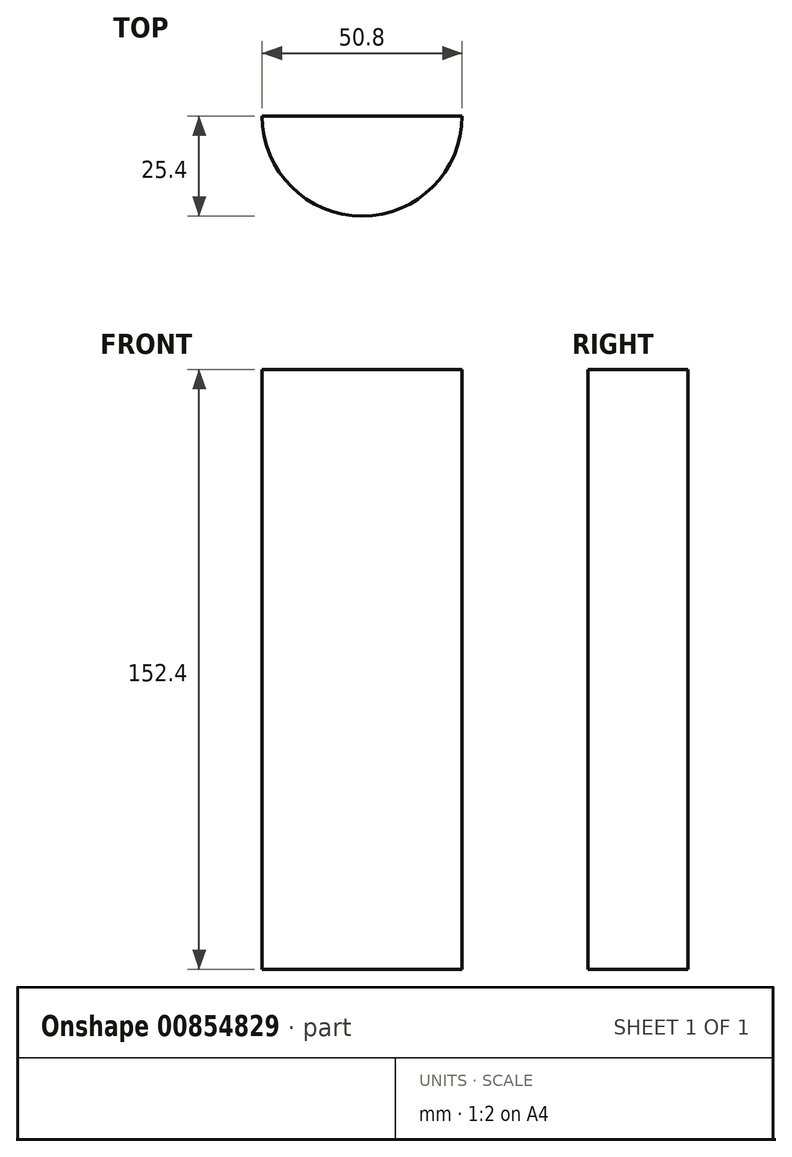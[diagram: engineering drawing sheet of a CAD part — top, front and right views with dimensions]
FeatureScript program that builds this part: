
annotation { "Feature Type Name" : "Feature", "Feature Type Description" : "" }
export const myFeature = defineFeature(function(context is Context, id is Id, definition is map)
    precondition{}
    {
        {
            var Q0;
            Q0=qCreatedBy(makeId("Top.planeOp"),FACE);
            var sketch = newSketch(context, id + "F0", { "sketchPlane" : qUnion([Q0])});
            skPoint(sketch, "E0", {"position": v(33.64, -34.66) * mm});
            skPoint(sketch, "E1", {"position": v(30.16, -37.73) * mm});
            skPoint(sketch, "E2", {"position": v(17.36, -45.07) * mm});
            skPoint(sketch, "E3", {"position": v(0, -48.3) * mm});
            skPoint(sketch, "E4", {"position": v(-17.3, -45.1) * mm});
            skPoint(sketch, "E5", {"position": v(-26.75, -40.22) * mm});
            skPoint(sketch, "E6", {"position": v(-47.04, -10.96) * mm});
            skLineSegment(sketch, "E7", {"start": v(-47.04, -10.96) * mm, "end": v(0, 0) * mm, "construction": true});
            skLineSegment(sketch, "E8", {"start": v(0, 0) * mm, "end": v(-26.75, -40.22) * mm, "construction": true});
            skLineSegment(sketch, "E9", {"start": v(0, 0) * mm, "end": v(-17.3, -45.1) * mm, "construction": true});
            skLineSegment(sketch, "E10", {"start": v(0, 0) * mm, "end": v(0, -48.3) * mm, "construction": true});
            skLineSegment(sketch, "E11", {"start": v(0, 0) * mm, "end": v(17.36, -45.07) * mm, "construction": true});
            skLineSegment(sketch, "E12", {"start": v(0, 0) * mm, "end": v(30.16, -37.73) * mm, "construction": true});
            skLineSegment(sketch, "E13", {"start": v(0, 0) * mm, "end": v(33.64, -34.66) * mm, "construction": true});
            skCircle(sketch, "E14", {"center": v(0, 0) * mm, "radius": 48.3 * mm, "construction": true});
            skLineSegment(sketch, "E15", {"start": v(0, 0) * mm, "end": v(38.53, -29.12) * mm, "construction": true});
            skLineSegment(sketch, "E16", {"start": v(0, 0) * mm, "end": v(43.2, -21.6) * mm, "construction": true});
            skSolve(sketch);
        }
        {
            var Q0;
            Q0=qCreatedBy(makeId("Top.planeOp"),FACE);
            var sketch = newSketch(context, id + "F1", { "sketchPlane" : qUnion([Q0])});
            skArc(sketch, "E17", {"start": v(-25.4, 0) * mm, "mid": v(0, -25.4) * mm, "end": v(25.4, 0) * mm});
            skLineSegment(sketch, "E18", {"start": v(-25.4, 0) * mm, "end": v(25.4, 0) * mm});
            skSolve(sketch);
        }
        {
            var Q0;
            Q0=makeQuery(id+"F1.imprint","IMPRINT",FACE,{"disambiguationData":[TD([[makeQuery(id+"F1.imprint","IMPRINT",EDGE,{"derivedFrom":sQuery(id+"F1.wireOp",EDGE,"E17")}),1.0]])]});
            var Q1;
            Q1=sQuery(id+"F1.wireOp",EDGE,"E17");
            extrude(context, id + "F2", {"entities" : qUnion([Q0]), "surfaceEntities" : qUnion([Q1]), "depth" : 152.4 * mm, "offsetDistance" : 25.4 * mm});
        }
        {
            var Q0;
            Q0=sQuery(id+"F0.wireOp",VERTEX,"E16.end");
            var Q1;
            Q1=sQuery(id+"F0.wireOp",EDGE,"E16");
            cPlane(context, id + "F3", {"entities" : qUnion([Q0, Q1]), "cplaneType" : CPlaneType.LINE_POINT, "offset" : 25.4 * mm, "width" : 152.4 * mm, "height" : 152.4 * mm});
        }
    });
